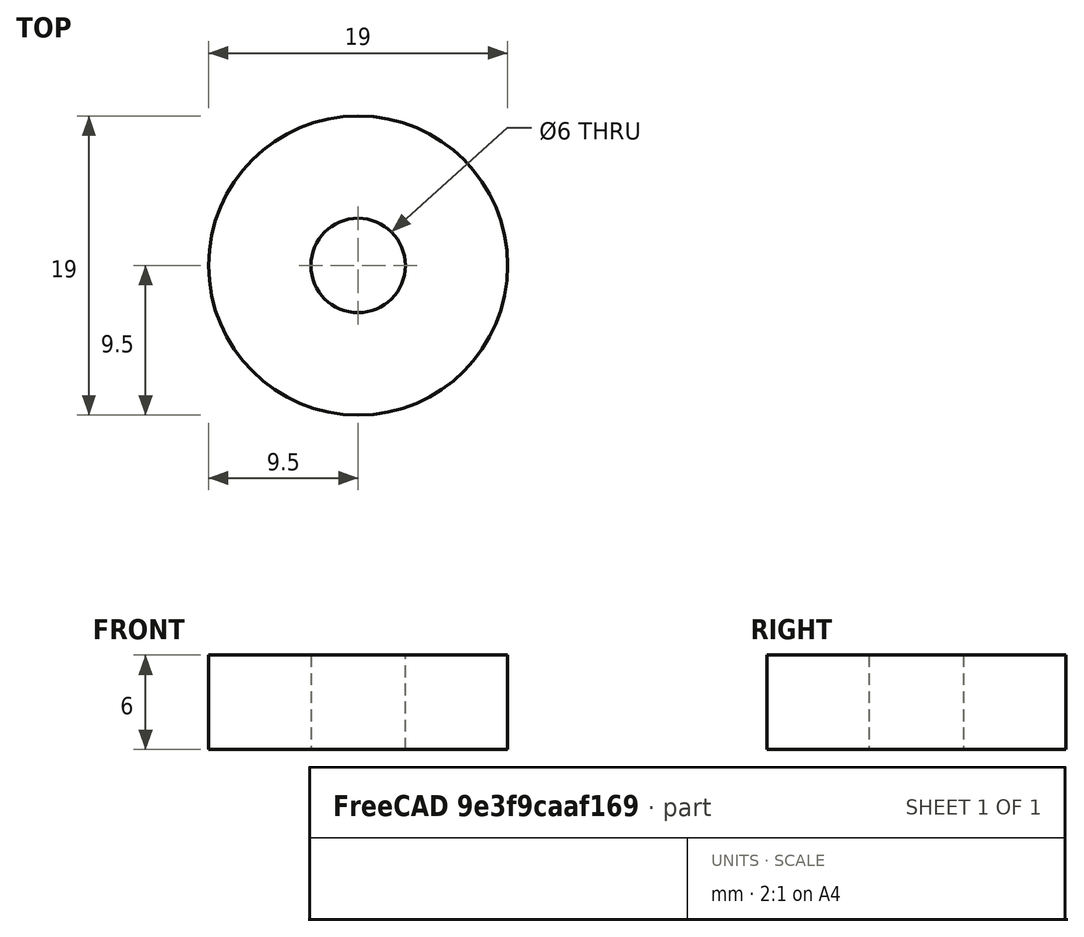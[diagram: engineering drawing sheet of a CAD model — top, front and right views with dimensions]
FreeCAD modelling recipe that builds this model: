
FCSTD DOCUMENT  (FreeCAD 0.18.4R)
Label: 6mm_Bearing
License: All rights reserved
LicenseURL: http://en.wikipedia.org/wiki/All_rights_reserved
objects: Sketcher::SketchObject×1, PartDesign::Pad×1, PartDesign::Body×1
note: 4 computed .brp shape members not serialized (recipe doc carries the construction recipe); baked Part::Feature solids carry a one-line shape summary decoded from their .brp

FEATURE [Sketcher::SketchObject] Sketch
  MapMode = 5
  Support = -> [XY_Plane]
  sketch-geometry (2):
    g0: Circle CenterX=0 CenterY=0 CenterZ=0 NormalX=0 NormalY=0 NormalZ=1 AngleXU=0 Radius=9.5
    g1: Circle CenterX=0 CenterY=0 CenterZ=0 NormalX=0 NormalY=0 NormalZ=1 AngleXU=0 Radius=3
  constraints (4):
    c: Coincident(g0,g-1)
    c: Coincident(g0,g1)
    c: Diameter(g1) = 6
    c: Diameter(g0) = 19
FEATURE [PartDesign::Pad] Pad
  Length = 6
  Length2 = 100
  Profile = -> Sketch
  Type = 0
FEATURE [PartDesign::Body] Body  label="6mm_bearing"
  Group = -> [Sketch,Pad]
  Origin = -> Origin
  Tip = -> Pad
